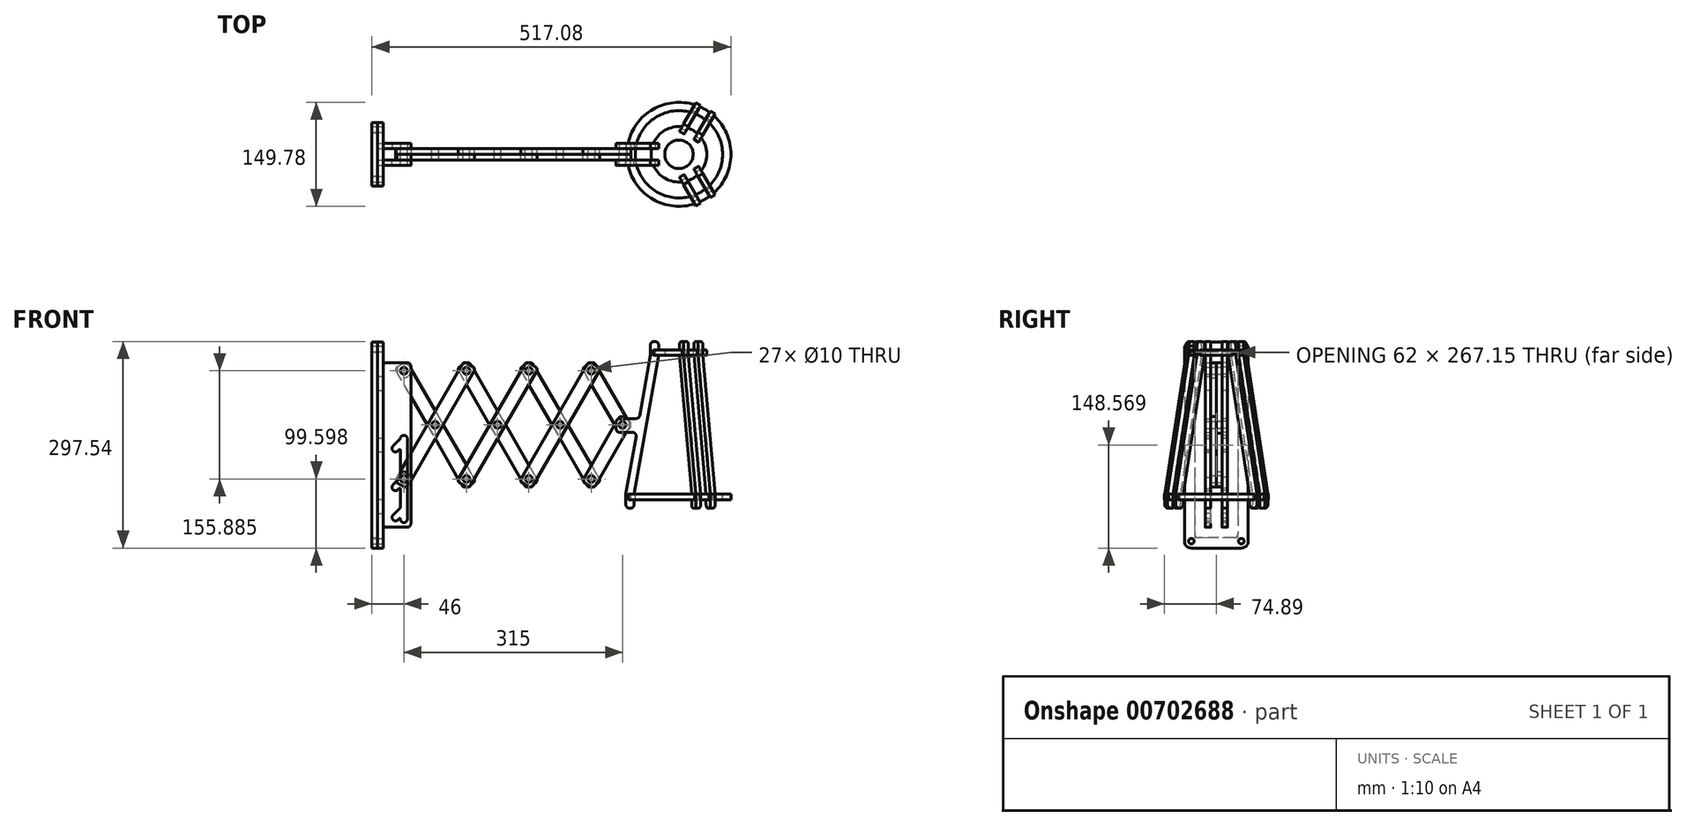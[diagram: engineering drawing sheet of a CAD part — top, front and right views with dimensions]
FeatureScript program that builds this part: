
annotation { "Feature Type Name" : "Feature", "Feature Type Description" : "" }
export const myFeature = defineFeature(function(context is Context, id is Id, definition is map)
    precondition{}
    {
        {
            var Q0;
            Q0=qCreatedBy(makeId("Front.planeOp"),FACE);
            var sketch = newSketch(context, id + "F0", { "sketchPlane" : qUnion([Q0])});
            skLineSegment(sketch, "E0.bottom", {"start": v(54.33, 84.1) * mm, "end": v(45.67, 89.1) * mm});
            skLineSegment(sketch, "E0.top", {"start": v(-45.67, -89.1) * mm, "end": v(-54.33, -84.1) * mm});
            skLineSegment(sketch, "E0.left", {"start": v(56.16, 77.27) * mm, "end": v(-38.84, -87.27) * mm});
            skLineSegment(sketch, "E0.right", {"start": v(38.84, 87.27) * mm, "end": v(-56.16, -77.27) * mm});
            skPoint(sketch, "E0.middle", {"position": v(0, 0) * mm});
            skLineSegment(sketch, "E1", {"start": v(0, 185.82) * mm, "end": v(0, -203.94) * mm, "construction": true});
            skLineSegment(sketch, "E2", {"start": v(-279.88, 0) * mm, "end": v(337.24, 0) * mm, "construction": true});
            skCircle(sketch, "E3", {"center": v(0, 0) * mm, "radius": 5 * mm});
            skCircle(sketch, "E4", {"center": v(45, 77.94) * mm, "radius": 5 * mm});
            skCircle(sketch, "E5.MirrorC", {"center": v(-45, -77.94) * mm, "radius": 5 * mm});
            skPoint(sketch, "E6.visualSharp", {"position": v(41.34, 91.6) * mm});
            skArc(sketch, "E6.filletArc", {"start": v(45.67, 89.1) * mm, "mid": v(41.88, 89.6) * mm, "end": v(38.84, 87.27) * mm});
            skPoint(sketch, "E7.visualSharp", {"position": v(58.66, 81.6) * mm});
            skArc(sketch, "E7.filletArc", {"start": v(56.16, 77.27) * mm, "mid": v(56.66, 81.07) * mm, "end": v(54.33, 84.1) * mm});
            skPoint(sketch, "E8.visualSharp", {"position": v(-41.34, -91.6) * mm});
            skArc(sketch, "E8.filletArc", {"start": v(-45.67, -89.1) * mm, "mid": v(-41.88, -89.6) * mm, "end": v(-38.84, -87.27) * mm});
            skPoint(sketch, "E9.visualSharp", {"position": v(-58.66, -81.6) * mm});
            skArc(sketch, "E9.filletArc", {"start": v(-56.16, -77.27) * mm, "mid": v(-56.66, -81.07) * mm, "end": v(-54.33, -84.1) * mm});
            skSolve(sketch);
        }
        {
            var Q0;
            Q0=makeQuery(id+"F0.imprint","IMPRINT",FACE,{"disambiguationData":[TD([[makeQuery(id+"F0.imprint","IMPRINT",EDGE,{"derivedFrom":sQuery(id+"F0.wireOp",EDGE,"E0.bottom")}),1.0]])]});
            var Q1;
            Q1=makeQuery(id+"F0.imprint","IMPRINT",FACE,{"disambiguationData":[TD([[makeQuery(id+"F0.imprint","IMPRINT",EDGE,{"derivedFrom":sQuery(id+"F0.wireOp",EDGE,"E3")}),-1.0]])]});
            var Q2;
            Q2=makeQuery(id+"F0.imprint","IMPRINT",FACE,{"disambiguationData":[TD([[makeQuery(id+"F0.imprint","IMPRINT",EDGE,{"derivedFrom":sQuery(id+"F0.wireOp",EDGE,"E0.top")}),-1.0]])]});
            var Q3;
            Q3=sQuery(id+"F0.wireOp",EDGE,"E0.right");
            var Q4;
            Q4=sQuery(id+"F0.wireOp",EDGE,"E0.left");
            extrude(context, id + "F1", {"entities" : qUnion([Q0, Q1, Q2]), "surfaceEntities" : qUnion([Q3, Q4]), "depth" : 8 * mm, "offsetDistance" : 25 * mm});
        }
        {
            var Q0;
            Q0=makeQuery(id+"F1.opExtrude","SWEPT_BODY",BODY,{"disambiguationData":[OSD([sQuery(id+"F0.wireOp",EDGE,"E0.bottom"),sQuery(id+"F0.wireOp",EDGE,"E0.top"),sQuery(id+"F0.wireOp",EDGE,"E0.left"),sQuery(id+"F0.wireOp",EDGE,"E0.right"),sQuery(id+"F0.wireOp",EDGE,"E3"),sQuery(id+"F0.wireOp",EDGE,"E4"),sQuery(id+"F0.wireOp",EDGE,"E5.MirrorC"),sQuery(id+"F0.wireOp",EDGE,"E6.filletArc"),sQuery(id+"F0.wireOp",EDGE,"E7.filletArc"),sQuery(id+"F0.wireOp",EDGE,"E8.filletArc"),sQuery(id+"F0.wireOp",EDGE,"E9.filletArc")])]});
            var Q1;
            Q1=qCreatedBy(makeId("Right.planeOp"),FACE);
            mirror(context, id + "F2", {"entities" : qUnion([Q0]), "mirrorPlane" : qUnion([Q1])});
        }
        {
            var Q0;
            Q0=makeQuery(id+"F2.opPattern","COPY",BODY,{"derivedFrom":makeQuery(id+"F1.opExtrude","SWEPT_BODY",BODY,{"disambiguationData":[OSD([sQuery(id+"F0.wireOp",EDGE,"E0.bottom"),sQuery(id+"F0.wireOp",EDGE,"E0.top"),sQuery(id+"F0.wireOp",EDGE,"E0.left"),sQuery(id+"F0.wireOp",EDGE,"E0.right"),sQuery(id+"F0.wireOp",EDGE,"E3"),sQuery(id+"F0.wireOp",EDGE,"E4"),sQuery(id+"F0.wireOp",EDGE,"E5.MirrorC"),sQuery(id+"F0.wireOp",EDGE,"E6.filletArc"),sQuery(id+"F0.wireOp",EDGE,"E7.filletArc"),sQuery(id+"F0.wireOp",EDGE,"E8.filletArc"),sQuery(id+"F0.wireOp",EDGE,"E9.filletArc")])]}),"instanceName":"1"});
            transform(context, id + "F3", {"entities" : qUnion([Q0]), "transformType" : TransformType.TRANSLATION_3D, "dx" : 0 * mm, "dy" : 8 * mm, "dz" : 0 * mm, "makeCopy" : false});
        }
        {
            var Q0;
            Q0=makeQuery(id+"F1.opExtrude","SWEPT_BODY",BODY,{"disambiguationData":[OSD([sQuery(id+"F0.wireOp",EDGE,"E0.bottom"),sQuery(id+"F0.wireOp",EDGE,"E0.top"),sQuery(id+"F0.wireOp",EDGE,"E0.left"),sQuery(id+"F0.wireOp",EDGE,"E0.right"),sQuery(id+"F0.wireOp",EDGE,"E3"),sQuery(id+"F0.wireOp",EDGE,"E4"),sQuery(id+"F0.wireOp",EDGE,"E5.MirrorC"),sQuery(id+"F0.wireOp",EDGE,"E6.filletArc"),sQuery(id+"F0.wireOp",EDGE,"E7.filletArc"),sQuery(id+"F0.wireOp",EDGE,"E8.filletArc"),sQuery(id+"F0.wireOp",EDGE,"E9.filletArc")])]});
            transform(context, id + "F4", {"entities" : qUnion([Q0]), "transformType" : TransformType.TRANSLATION_3D, "dx" : 90 * mm, "dy" : 0 * mm, "dz" : 0 * mm, "makeCopy" : true});
        }
        {
            var Q0;
            Q0=makeQuery(id+"F2.opPattern","COPY",BODY,{"derivedFrom":makeQuery(id+"F1.opExtrude","SWEPT_BODY",BODY,{"disambiguationData":[OSD([sQuery(id+"F0.wireOp",EDGE,"E0.bottom"),sQuery(id+"F0.wireOp",EDGE,"E0.top"),sQuery(id+"F0.wireOp",EDGE,"E0.left"),sQuery(id+"F0.wireOp",EDGE,"E0.right"),sQuery(id+"F0.wireOp",EDGE,"E3"),sQuery(id+"F0.wireOp",EDGE,"E4"),sQuery(id+"F0.wireOp",EDGE,"E5.MirrorC"),sQuery(id+"F0.wireOp",EDGE,"E6.filletArc"),sQuery(id+"F0.wireOp",EDGE,"E7.filletArc"),sQuery(id+"F0.wireOp",EDGE,"E8.filletArc"),sQuery(id+"F0.wireOp",EDGE,"E9.filletArc")])]}),"instanceName":"1"});
            transform(context, id + "F5", {"entities" : qUnion([Q0]), "transformType" : TransformType.TRANSLATION_3D, "dx" : -90 * mm, "dy" : 0 * mm, "dz" : 0 * mm, "makeCopy" : true});
        }
        {
            var Q0;
            Q0=makeQuery(id+"F1.opExtrude","SWEPT_BODY",BODY,{"disambiguationData":[OSD([sQuery(id+"F0.wireOp",EDGE,"E0.bottom"),sQuery(id+"F0.wireOp",EDGE,"E0.top"),sQuery(id+"F0.wireOp",EDGE,"E0.left"),sQuery(id+"F0.wireOp",EDGE,"E0.right"),sQuery(id+"F0.wireOp",EDGE,"E3"),sQuery(id+"F0.wireOp",EDGE,"E4"),sQuery(id+"F0.wireOp",EDGE,"E5.MirrorC"),sQuery(id+"F0.wireOp",EDGE,"E6.filletArc"),sQuery(id+"F0.wireOp",EDGE,"E7.filletArc"),sQuery(id+"F0.wireOp",EDGE,"E8.filletArc"),sQuery(id+"F0.wireOp",EDGE,"E9.filletArc")])]});
            transform(context, id + "F6", {"entities" : qUnion([Q0]), "transformType" : TransformType.TRANSLATION_3D, "dx" : -90 * mm, "dy" : 0 * mm, "dz" : 0 * mm, "makeCopy" : true});
        }
        {
            var Q0;
            Q0=makeQuery(id+"F2.opPattern","COPY",BODY,{"derivedFrom":makeQuery(id+"F1.opExtrude","SWEPT_BODY",BODY,{"disambiguationData":[OSD([sQuery(id+"F0.wireOp",EDGE,"E0.bottom"),sQuery(id+"F0.wireOp",EDGE,"E0.top"),sQuery(id+"F0.wireOp",EDGE,"E0.left"),sQuery(id+"F0.wireOp",EDGE,"E0.right"),sQuery(id+"F0.wireOp",EDGE,"E3"),sQuery(id+"F0.wireOp",EDGE,"E4"),sQuery(id+"F0.wireOp",EDGE,"E5.MirrorC"),sQuery(id+"F0.wireOp",EDGE,"E6.filletArc"),sQuery(id+"F0.wireOp",EDGE,"E7.filletArc"),sQuery(id+"F0.wireOp",EDGE,"E8.filletArc"),sQuery(id+"F0.wireOp",EDGE,"E9.filletArc")])]}),"instanceName":"1"});
            transform(context, id + "F7", {"entities" : qUnion([Q0]), "transformType" : TransformType.TRANSLATION_3D, "dx" : 90 * mm, "dy" : 0 * mm, "dz" : 0 * mm, "makeCopy" : true});
        }
        {
            var Q0;
            Q0=makeQuery(id+"F7.opPattern","COPY",FACE,{"derivedFrom":makeQuery(id+"F2.opPattern","COPY",FACE,{"derivedFrom":makeQuery(id+"F1.opExtrude","CAP_FACE",FACE,{"disambiguationData":[OSD([sQuery(id+"F0.wireOp",EDGE,"E0.bottom"),sQuery(id+"F0.wireOp",EDGE,"E0.top"),sQuery(id+"F0.wireOp",EDGE,"E0.left"),sQuery(id+"F0.wireOp",EDGE,"E0.right"),sQuery(id+"F0.wireOp",EDGE,"E3"),sQuery(id+"F0.wireOp",EDGE,"E4"),sQuery(id+"F0.wireOp",EDGE,"E5.MirrorC"),sQuery(id+"F0.wireOp",EDGE,"E6.filletArc"),sQuery(id+"F0.wireOp",EDGE,"E7.filletArc"),sQuery(id+"F0.wireOp",EDGE,"E8.filletArc"),sQuery(id+"F0.wireOp",EDGE,"E9.filletArc")])],"isStart":true}),"instanceName":"1"}),"instanceName":"1"});
            var sketch = newSketch(context, id + "F8", { "sketchPlane" : qUnion([Q0])});
            skCircle(sketch, "E10.0", {"center": v(135, 77.94) * mm, "radius": 5 * mm});
            skLineSegment(sketch, "E11", {"start": v(130, 89.6) * mm, "end": v(160, 89.6) * mm, "construction": true});
            skPoint(sketch, "E11.startSnap0", {"position": v(41.88, 89.6) * mm});
            skLineSegment(sketch, "E12", {"start": v(22.72, 0) * mm, "end": v(188.2, 0) * mm, "construction": true});
            skLineSegment(sketch, "E13", {"start": v(130, 89.6) * mm, "end": v(160, 89.6) * mm});
            skLineSegment(sketch, "E14", {"start": v(135, 121.8) * mm, "end": v(135, -172.81) * mm, "construction": true});
            skArc(sketch, "E15.0", {"start": v(140, -20) * mm, "mid": v(135, -15) * mm, "end": v(130, -20) * mm});
            skLineSegment(sketch, "E16", {"start": v(95.12, -77.94) * mm, "end": v(188.2, -77.94) * mm, "construction": true});
            skArc(sketch, "E17.MirrorC", {"start": v(140, -135.88) * mm, "mid": v(135, -140.88) * mm, "end": v(130, -135.88) * mm});
            skLineSegment(sketch, "E18", {"start": v(130, -147.54) * mm, "end": v(160, -147.54) * mm});
            skLineSegment(sketch, "E19", {"start": v(125, 84.6) * mm, "end": v(125, -142.54) * mm});
            skLineSegment(sketch, "E20", {"start": v(165, 84.6) * mm, "end": v(165, 69.6) * mm});
            skLineSegment(sketch, "E21", {"start": v(130, -135.88) * mm, "end": v(130, -20) * mm});
            skLineSegment(sketch, "E22.MirrorCS", {"start": v(140, -119.33) * mm, "end": v(140, -92.37) * mm});
            skPoint(sketch, "E23.newPointB", {"position": v(24.22, 89.6) * mm});
            skArc(sketch, "E23.filletArc", {"start": v(130, 89.6) * mm, "mid": v(126.46, 88.14) * mm, "end": v(125, 84.6) * mm});
            skPoint(sketch, "E24.newPointA", {"position": v(188.2, 89.6) * mm});
            skArc(sketch, "E24.filletArc", {"start": v(165, 84.6) * mm, "mid": v(163.54, 88.14) * mm, "end": v(160, 89.6) * mm});
            skPoint(sketch, "E25.visualSharp", {"position": v(125, -147.54) * mm});
            skArc(sketch, "E25.filletArc", {"start": v(125, -142.54) * mm, "mid": v(126.46, -146.08) * mm, "end": v(130, -147.54) * mm});
            skPoint(sketch, "E26.visualSharp", {"position": v(165, -147.54) * mm});
            skArc(sketch, "E26.filletArc", {"start": v(160, -147.54) * mm, "mid": v(163.54, -146.08) * mm, "end": v(165, -142.54) * mm});
            skLineSegment(sketch, "E27", {"start": v(165, 69.6) * mm, "end": v(173, 69.6) * mm});
            skLineSegment(sketch, "E28", {"start": v(173, 69.6) * mm, "end": v(173, 49.6) * mm});
            skLineSegment(sketch, "E29", {"start": v(173, 49.6) * mm, "end": v(165, 49.6) * mm});
            skLineSegment(sketch, "E30", {"start": v(165, -107.54) * mm, "end": v(173, -107.54) * mm});
            skLineSegment(sketch, "E31", {"start": v(173, -107.54) * mm, "end": v(173, -127.54) * mm});
            skLineSegment(sketch, "E32", {"start": v(173, -127.54) * mm, "end": v(165, -127.54) * mm});
            skLineSegment(sketch, "E33.trimOffspring", {"start": v(165, -127.54) * mm, "end": v(165, -142.54) * mm});
            skLineSegment(sketch, "E34.trimOffspring", {"start": v(165, 49.6) * mm, "end": v(165, -18.97) * mm});
            skLineSegment(sketch, "E35", {"start": v(165, -18.97) * mm, "end": v(173, -18.97) * mm});
            skLineSegment(sketch, "E36", {"start": v(173, -18.97) * mm, "end": v(173, -38.97) * mm});
            skLineSegment(sketch, "E37", {"start": v(173, -38.97) * mm, "end": v(165, -38.97) * mm});
            skLineSegment(sketch, "E38.trimOffspring", {"start": v(165, -38.97) * mm, "end": v(165, -107.54) * mm});
            skPoint(sketch, "E39.orphan", {"position": v(165, -28.97) * mm});
            skArc(sketch, "E40", {"start": v(143.5, -93.46) * mm, "mid": v(150.57, -93.46) * mm, "end": v(150.57, -86.4) * mm});
            skLineSegment(sketch, "E41", {"start": v(150.57, -86.4) * mm, "end": v(140, -75.82) * mm});
            skLineSegment(sketch, "E42.MirrorCS", {"start": v(143.5, -93.46) * mm, "end": v(141.7, -91.67) * mm});
            skArc(sketch, "E43.filletArc", {"start": v(141.7, -91.67) * mm, "mid": v(140.62, -91.45) * mm, "end": v(140, -92.37) * mm});
            skArc(sketch, "E44", {"start": v(143.5, -136.97) * mm, "mid": v(150.57, -136.97) * mm, "end": v(150.57, -129.9) * mm});
            skLineSegment(sketch, "E45", {"start": v(150.57, -129.9) * mm, "end": v(140, -119.33) * mm});
            skLineSegment(sketch, "E46.MirrorCS", {"start": v(143.5, -136.97) * mm, "end": v(141.7, -135.18) * mm});
            skArc(sketch, "E47.filletArc", {"start": v(141.7, -135.18) * mm, "mid": v(140.62, -134.96) * mm, "end": v(140, -135.88) * mm});
            skArc(sketch, "E48", {"start": v(143.5, -37.65) * mm, "mid": v(150.57, -37.65) * mm, "end": v(150.57, -30.57) * mm});
            skLineSegment(sketch, "E49", {"start": v(150.57, -30.57) * mm, "end": v(140, -20) * mm});
            skLineSegment(sketch, "E50.MirrorCS", {"start": v(143.5, -37.65) * mm, "end": v(141.7, -35.85) * mm});
            skArc(sketch, "E51.filletArc", {"start": v(141.7, -35.85) * mm, "mid": v(140.62, -35.63) * mm, "end": v(140, -36.56) * mm});
            skLineSegment(sketch, "E52.trimOffspring", {"start": v(140, -75.82) * mm, "end": v(140, -36.56) * mm});
            skSolve(sketch);
        }
        {
            var Q0;
            Q0 = qSketchRegion(id + "F8", true);
            extrude(context, id + "F9", {"entities" : qUnion([Q0]), "depth" : 8 * mm, "offsetDistance" : 25 * mm});
        }
        {
            var Q0;
            Q0=makeQuery(id+"F9.opExtrude","SWEPT_BODY",BODY,{"disambiguationData":[OSD([sQuery(id+"F8.wireOp",EDGE,"E10.0"),sQuery(id+"F8.wireOp",EDGE,"E13"),sQuery(id+"F8.wireOp",EDGE,"E15.0"),sQuery(id+"F8.wireOp",EDGE,"E17.MirrorC"),sQuery(id+"F8.wireOp",EDGE,"E18"),sQuery(id+"F8.wireOp",EDGE,"E19"),sQuery(id+"F8.wireOp",EDGE,"E20"),sQuery(id+"F8.wireOp",EDGE,"E21"),sQuery(id+"F8.wireOp",EDGE,"E22.MirrorCS"),sQuery(id+"F8.wireOp",EDGE,"E23.filletArc"),sQuery(id+"F8.wireOp",EDGE,"E24.filletArc"),sQuery(id+"F8.wireOp",EDGE,"E25.filletArc"),sQuery(id+"F8.wireOp",EDGE,"E26.filletArc")])]});
            var Q1;
            Q1=qCreatedBy(makeId("Front.planeOp"),FACE);
            mirror(context, id + "F10", {"entities" : qUnion([Q0]), "mirrorPlane" : qUnion([Q1])});
        }
        {
            var Q0;
            Q0=makeQuery(id+"F9.opExtrude","SWEPT_FACE",FACE,{"disambiguationData":[OSD([sQuery(id+"F8.wireOp",EDGE,"E34.trimOffspring")])]});
            var sketch = newSketch(context, id + "F11", { "sketchPlane" : qUnion([Q0])});
            skPoint(sketch, "E53.middle", {"position": v(0, 0) * mm});
            skLineSegment(sketch, "E54.0.0", {"start": v(-8, 49.6) * mm, "end": v(-8, 69.6) * mm});
            skLineSegment(sketch, "E54.0.1", {"start": v(-8, 69.6) * mm, "end": v(-16, 69.6) * mm});
            skLineSegment(sketch, "E54.0.2", {"start": v(-16, 69.6) * mm, "end": v(-16, 49.6) * mm});
            skLineSegment(sketch, "E54.0.3", {"start": v(-16, 49.6) * mm, "end": v(-8, 49.6) * mm});
            skLineSegment(sketch, "E55.0.0", {"start": v(8, 69.6) * mm, "end": v(8, 49.6) * mm});
            skLineSegment(sketch, "E55.0.1", {"start": v(8, 49.6) * mm, "end": v(16, 49.6) * mm});
            skLineSegment(sketch, "E55.0.2", {"start": v(16, 49.6) * mm, "end": v(16, 69.6) * mm});
            skLineSegment(sketch, "E55.0.3", {"start": v(16, 69.6) * mm, "end": v(8, 69.6) * mm});
            skLineSegment(sketch, "E56.0.0", {"start": v(-8, -38.97) * mm, "end": v(-8, -18.97) * mm});
            skLineSegment(sketch, "E56.0.1", {"start": v(-8, -18.97) * mm, "end": v(-16, -18.97) * mm});
            skLineSegment(sketch, "E56.0.2", {"start": v(-16, -18.97) * mm, "end": v(-16, -38.97) * mm});
            skLineSegment(sketch, "E56.0.3", {"start": v(-16, -38.97) * mm, "end": v(-8, -38.97) * mm});
            skLineSegment(sketch, "E57.0.0", {"start": v(8, -18.97) * mm, "end": v(8, -38.97) * mm});
            skLineSegment(sketch, "E57.0.1", {"start": v(8, -38.97) * mm, "end": v(16, -38.97) * mm});
            skLineSegment(sketch, "E57.0.2", {"start": v(16, -38.97) * mm, "end": v(16, -18.97) * mm});
            skLineSegment(sketch, "E57.0.3", {"start": v(16, -18.97) * mm, "end": v(8, -18.97) * mm});
            skLineSegment(sketch, "E58.0.0", {"start": v(-8, -127.54) * mm, "end": v(-8, -107.54) * mm});
            skLineSegment(sketch, "E58.0.1", {"start": v(-8, -107.54) * mm, "end": v(-16, -107.54) * mm});
            skLineSegment(sketch, "E58.0.2", {"start": v(-16, -107.54) * mm, "end": v(-16, -127.54) * mm});
            skLineSegment(sketch, "E58.0.3", {"start": v(-16, -127.54) * mm, "end": v(-8, -127.54) * mm});
            skLineSegment(sketch, "E59.0.0", {"start": v(8, -107.54) * mm, "end": v(8, -127.54) * mm});
            skLineSegment(sketch, "E59.0.1", {"start": v(8, -127.54) * mm, "end": v(16, -127.54) * mm});
            skLineSegment(sketch, "E59.0.2", {"start": v(16, -127.54) * mm, "end": v(16, -107.54) * mm});
            skLineSegment(sketch, "E59.0.3", {"start": v(16, -107.54) * mm, "end": v(8, -107.54) * mm});
            skLineSegment(sketch, "E60", {"start": v(46, 109.6) * mm, "end": v(46, -167.54) * mm});
            skLineSegment(sketch, "E61", {"start": v(-36, 119.6) * mm, "end": v(36, 119.6) * mm});
            skLineSegment(sketch, "E62", {"start": v(-36, -177.54) * mm, "end": v(36, -177.54) * mm});
            skLineSegment(sketch, "E63.MirrorCS", {"start": v(-46, 109.6) * mm, "end": v(-46, -167.54) * mm});
            skPoint(sketch, "E64.visualSharp", {"position": v(-46, 119.6) * mm});
            skArc(sketch, "E64.filletArc", {"start": v(-36, 119.6) * mm, "mid": v(-43.07, 116.67) * mm, "end": v(-46, 109.6) * mm});
            skPoint(sketch, "E65.visualSharp", {"position": v(46, 119.6) * mm});
            skArc(sketch, "E65.filletArc", {"start": v(46, 109.6) * mm, "mid": v(43.07, 116.67) * mm, "end": v(36, 119.6) * mm});
            skPoint(sketch, "E66.visualSharp", {"position": v(-46, -177.54) * mm});
            skArc(sketch, "E66.filletArc", {"start": v(-46, -167.54) * mm, "mid": v(-43.07, -174.62) * mm, "end": v(-36, -177.54) * mm});
            skPoint(sketch, "E67.visualSharp", {"position": v(46, -177.54) * mm});
            skArc(sketch, "E67.filletArc", {"start": v(36, -177.54) * mm, "mid": v(43.07, -174.62) * mm, "end": v(46, -167.54) * mm});
            skCircle(sketch, "E68", {"center": v(-36, 109.6) * mm, "radius": 4 * mm});
            skCircle(sketch, "E69", {"center": v(36, 109.6) * mm, "radius": 4 * mm});
            skCircle(sketch, "E70", {"center": v(-36, -167.54) * mm, "radius": 4 * mm});
            skCircle(sketch, "E71", {"center": v(36, -167.54) * mm, "radius": 4 * mm});
            skSolve(sketch);
        }
        {
            var Q0;
            Q0 = qSketchRegion(id + "F11", true);
            extrude(context, id + "F12", {"entities" : qUnion([Q0]), "depth" : 8 * mm, "offsetDistance" : 25 * mm});
        }
        {
            var Q0;
            Q0=makeQuery(id+"F12.opExtrude","CAP_FACE",FACE,{"disambiguationData":[OSD([sQuery(id+"F11.wireOp",EDGE,"E54.0.0"),sQuery(id+"F11.wireOp",EDGE,"E54.0.1"),sQuery(id+"F11.wireOp",EDGE,"E54.0.2"),sQuery(id+"F11.wireOp",EDGE,"E54.0.3"),sQuery(id+"F11.wireOp",EDGE,"E55.0.0"),sQuery(id+"F11.wireOp",EDGE,"E55.0.1"),sQuery(id+"F11.wireOp",EDGE,"E55.0.2"),sQuery(id+"F11.wireOp",EDGE,"E55.0.3"),sQuery(id+"F11.wireOp",EDGE,"E56.0.0"),sQuery(id+"F11.wireOp",EDGE,"E56.0.1"),sQuery(id+"F11.wireOp",EDGE,"E56.0.2"),sQuery(id+"F11.wireOp",EDGE,"E56.0.3"),sQuery(id+"F11.wireOp",EDGE,"E57.0.0"),sQuery(id+"F11.wireOp",EDGE,"E57.0.1"),sQuery(id+"F11.wireOp",EDGE,"E57.0.2"),sQuery(id+"F11.wireOp",EDGE,"E57.0.3"),sQuery(id+"F11.wireOp",EDGE,"E58.0.0"),sQuery(id+"F11.wireOp",EDGE,"E58.0.1"),sQuery(id+"F11.wireOp",EDGE,"E58.0.2"),sQuery(id+"F11.wireOp",EDGE,"E58.0.3"),sQuery(id+"F11.wireOp",EDGE,"E59.0.0"),sQuery(id+"F11.wireOp",EDGE,"E59.0.1"),sQuery(id+"F11.wireOp",EDGE,"E59.0.2"),sQuery(id+"F11.wireOp",EDGE,"E59.0.3"),sQuery(id+"F11.wireOp",EDGE,"E60"),sQuery(id+"F11.wireOp",EDGE,"E61"),sQuery(id+"F11.wireOp",EDGE,"E62"),sQuery(id+"F11.wireOp",EDGE,"E63.MirrorCS"),sQuery(id+"F11.wireOp",EDGE,"E64.filletArc"),sQuery(id+"F11.wireOp",EDGE,"E65.filletArc"),sQuery(id+"F11.wireOp",EDGE,"E66.filletArc"),sQuery(id+"F11.wireOp",EDGE,"E67.filletArc"),sQuery(id+"F11.wireOp",EDGE,"E68"),sQuery(id+"F11.wireOp",EDGE,"E69"),sQuery(id+"F11.wireOp",EDGE,"E70"),sQuery(id+"F11.wireOp",EDGE,"E71")])],"isStart":false});
            var sketch = newSketch(context, id + "F13", { "sketchPlane" : qUnion([Q0])});
            skArc(sketch, "E72.0.0", {"start": v(-36, 119.6) * mm, "mid": v(-43.07, 116.67) * mm, "end": v(-46, 109.6) * mm});
            skLineSegment(sketch, "E72.0.1", {"start": v(-46, 109.6) * mm, "end": v(-46, -167.54) * mm});
            skArc(sketch, "E72.0.2", {"start": v(-46, -167.54) * mm, "mid": v(-43.07, -174.62) * mm, "end": v(-36, -177.54) * mm});
            skLineSegment(sketch, "E72.0.3", {"start": v(-36, -177.54) * mm, "end": v(36, -177.54) * mm});
            skArc(sketch, "E72.0.4", {"start": v(36, -177.54) * mm, "mid": v(43.07, -174.62) * mm, "end": v(46, -167.54) * mm});
            skLineSegment(sketch, "E72.0.5", {"start": v(46, -167.54) * mm, "end": v(46, 109.6) * mm});
            skArc(sketch, "E72.0.6", {"start": v(46, 109.6) * mm, "mid": v(43.07, 116.67) * mm, "end": v(36, 119.6) * mm});
            skLineSegment(sketch, "E72.0.7", {"start": v(36, 119.6) * mm, "end": v(-36, 119.6) * mm});
            skCircle(sketch, "E73.0", {"center": v(-36, 109.6) * mm, "radius": 4 * mm});
            skCircle(sketch, "E74.0", {"center": v(36, 109.6) * mm, "radius": 4 * mm});
            skCircle(sketch, "E75.0", {"center": v(-36, -167.54) * mm, "radius": 4 * mm});
            skCircle(sketch, "E76.0", {"center": v(36, -167.54) * mm, "radius": 4 * mm});
            skLineSegment(sketch, "E77.bottom", {"start": v(-26, 104.6) * mm, "end": v(26, 104.6) * mm});
            skLineSegment(sketch, "E77.top", {"start": v(-26, -162.54) * mm, "end": v(26, -162.54) * mm});
            skLineSegment(sketch, "E77.left", {"start": v(-31, 99.6) * mm, "end": v(-31, -157.54) * mm});
            skLineSegment(sketch, "E77.right", {"start": v(31, 99.6) * mm, "end": v(31, -157.54) * mm});
            skPoint(sketch, "E78.visualSharp", {"position": v(-31, 104.6) * mm});
            skArc(sketch, "E78.filletArc", {"start": v(-26, 104.6) * mm, "mid": v(-29.54, 103.14) * mm, "end": v(-31, 99.6) * mm});
            skPoint(sketch, "E79.visualSharp", {"position": v(31, 104.6) * mm});
            skArc(sketch, "E79.filletArc", {"start": v(31, 99.6) * mm, "mid": v(29.54, 103.14) * mm, "end": v(26, 104.6) * mm});
            skPoint(sketch, "E80.visualSharp", {"position": v(-31, -162.54) * mm});
            skArc(sketch, "E80.filletArc", {"start": v(-31, -157.54) * mm, "mid": v(-29.54, -161.08) * mm, "end": v(-26, -162.54) * mm});
            skPoint(sketch, "E81.visualSharp", {"position": v(31, -162.54) * mm});
            skArc(sketch, "E81.filletArc", {"start": v(26, -162.54) * mm, "mid": v(29.54, -161.08) * mm, "end": v(31, -157.54) * mm});
            skSolve(sketch);
        }
        {
            var Q0;
            Q0 = qSketchRegion(id + "F13", true);
            extrude(context, id + "F14", {"entities" : qUnion([Q0]), "depth" : 8 * mm, "offsetDistance" : 25 * mm});
        }
        {
            var Q0;
            Q0=makeQuery(id+"F6.opPattern","COPY",FACE,{"derivedFrom":makeQuery(id+"F1.opExtrude","CAP_FACE",FACE,{"disambiguationData":[OSD([sQuery(id+"F0.wireOp",EDGE,"E0.bottom"),sQuery(id+"F0.wireOp",EDGE,"E0.top"),sQuery(id+"F0.wireOp",EDGE,"E0.left"),sQuery(id+"F0.wireOp",EDGE,"E0.right"),sQuery(id+"F0.wireOp",EDGE,"E3"),sQuery(id+"F0.wireOp",EDGE,"E4"),sQuery(id+"F0.wireOp",EDGE,"E5.MirrorC"),sQuery(id+"F0.wireOp",EDGE,"E6.filletArc"),sQuery(id+"F0.wireOp",EDGE,"E7.filletArc"),sQuery(id+"F0.wireOp",EDGE,"E8.filletArc"),sQuery(id+"F0.wireOp",EDGE,"E9.filletArc")])],"isStart":true}),"instanceName":"1"});
            var sketch = newSketch(context, id + "F15", { "sketchPlane" : qUnion([Q0])});
            skCircle(sketch, "E82.0", {"center": v(135, -77.94) * mm, "radius": 5 * mm});
            skCircle(sketch, "E83", {"center": v(135, -77.94) * mm, "radius": 10 * mm});
            skSolve(sketch);
        }
        {
            var Q0;
            Q0 = qSketchRegion(id + "F15", true);
            extrude(context, id + "F16", {"entities" : qUnion([Q0]), "depth" : 8 * mm, "offsetDistance" : 25 * mm});
        }
        {
            var Q0;
            Q0=makeQuery(id+"F5.opPattern","COPY",FACE,{"derivedFrom":makeQuery(id+"F2.opPattern","COPY",FACE,{"derivedFrom":makeQuery(id+"F1.opExtrude","CAP_FACE",FACE,{"disambiguationData":[OSD([sQuery(id+"F0.wireOp",EDGE,"E0.bottom"),sQuery(id+"F0.wireOp",EDGE,"E0.top"),sQuery(id+"F0.wireOp",EDGE,"E0.left"),sQuery(id+"F0.wireOp",EDGE,"E0.right"),sQuery(id+"F0.wireOp",EDGE,"E3"),sQuery(id+"F0.wireOp",EDGE,"E4"),sQuery(id+"F0.wireOp",EDGE,"E5.MirrorC"),sQuery(id+"F0.wireOp",EDGE,"E6.filletArc"),sQuery(id+"F0.wireOp",EDGE,"E7.filletArc"),sQuery(id+"F0.wireOp",EDGE,"E8.filletArc"),sQuery(id+"F0.wireOp",EDGE,"E9.filletArc")])],"isStart":false}),"instanceName":"1"}),"instanceName":"1"});
            var sketch = newSketch(context, id + "F17", { "sketchPlane" : qUnion([Q0])});
            skCircle(sketch, "E84.0", {"center": v(-135, 77.94) * mm, "radius": 5 * mm});
            skCircle(sketch, "E85", {"center": v(-135, 77.94) * mm, "radius": 10 * mm});
            skSolve(sketch);
        }
        {
            var Q0;
            Q0 = qSketchRegion(id + "F17", true);
            extrude(context, id + "F18", {"entities" : qUnion([Q0]), "depth" : 8 * mm, "offsetDistance" : 25 * mm});
        }
        {
            var Q0;
            Q0=makeQuery(id+"F2.opPattern","COPY",FACE,{"derivedFrom":makeQuery(id+"F1.opExtrude","CAP_FACE",FACE,{"disambiguationData":[OSD([sQuery(id+"F0.wireOp",EDGE,"E0.bottom"),sQuery(id+"F0.wireOp",EDGE,"E0.top"),sQuery(id+"F0.wireOp",EDGE,"E0.left"),sQuery(id+"F0.wireOp",EDGE,"E0.right"),sQuery(id+"F0.wireOp",EDGE,"E3"),sQuery(id+"F0.wireOp",EDGE,"E4"),sQuery(id+"F0.wireOp",EDGE,"E5.MirrorC"),sQuery(id+"F0.wireOp",EDGE,"E6.filletArc"),sQuery(id+"F0.wireOp",EDGE,"E7.filletArc"),sQuery(id+"F0.wireOp",EDGE,"E8.filletArc"),sQuery(id+"F0.wireOp",EDGE,"E9.filletArc")])],"isStart":false}),"instanceName":"1"});
            var sketch = newSketch(context, id + "F19", { "sketchPlane" : qUnion([Q0])});
            skLineSegment(sketch, "E86.top", {"start": v(134.33, -89.1) * mm, "end": v(125.67, -84.1) * mm});
            skLineSegment(sketch, "E86.left", {"start": v(191.55, 0) * mm, "end": v(141.16, -87.27) * mm});
            skLineSegment(sketch, "E86.right", {"start": v(173.84, 9.33) * mm, "end": v(123.84, -77.27) * mm});
            skPoint(sketch, "E86.middle", {"position": v(180, 0) * mm});
            skLineSegment(sketch, "E87", {"start": v(180, 185.82) * mm, "end": v(180, -203.94) * mm, "construction": true});
            skLineSegment(sketch, "E88", {"start": v(-99.88, 0) * mm, "end": v(517.24, 0) * mm, "construction": true});
            skCircle(sketch, "E89.MirrorC", {"center": v(135, -77.94) * mm, "radius": 5 * mm});
            skPoint(sketch, "E90.visualSharp", {"position": v(138.66, -91.6) * mm});
            skArc(sketch, "E90.filletArc", {"start": v(134.33, -89.1) * mm, "mid": v(138.12, -89.6) * mm, "end": v(141.16, -87.27) * mm});
            skPoint(sketch, "E91.visualSharp", {"position": v(121.34, -81.6) * mm});
            skArc(sketch, "E91.filletArc", {"start": v(123.84, -77.27) * mm, "mid": v(123.34, -81.07) * mm, "end": v(125.67, -84.1) * mm});
            skLineSegment(sketch, "E92.bottom", {"start": v(189.33, 6.16) * mm, "end": v(180.67, 11.16) * mm});
            skCircle(sketch, "E93", {"center": v(180, 0) * mm, "radius": 5 * mm});
            skArc(sketch, "E94.filletArc", {"start": v(180.67, 11.16) * mm, "mid": v(176.88, 11.66) * mm, "end": v(173.84, 9.33) * mm});
            skArc(sketch, "E95.filletArc", {"start": v(191.16, -0.67) * mm, "mid": v(191.66, 3.12) * mm, "end": v(189.33, 6.16) * mm});
            skSolve(sketch);
        }
        {
            var Q0;
            Q0 = qSketchRegion(id + "F19", true);
            extrude(context, id + "F20", {"entities" : qUnion([Q0]), "operationType" : NewBodyOperationType.ADD, "depth" : 8 * mm, "offsetDistance" : 25 * mm});
        }
        {
            var Q0;
            Q0=makeQuery(id+"F4.opPattern","COPY",FACE,{"derivedFrom":makeQuery(id+"F1.opExtrude","CAP_FACE",FACE,{"disambiguationData":[OSD([sQuery(id+"F0.wireOp",EDGE,"E0.bottom"),sQuery(id+"F0.wireOp",EDGE,"E0.top"),sQuery(id+"F0.wireOp",EDGE,"E0.left"),sQuery(id+"F0.wireOp",EDGE,"E0.right"),sQuery(id+"F0.wireOp",EDGE,"E3"),sQuery(id+"F0.wireOp",EDGE,"E4"),sQuery(id+"F0.wireOp",EDGE,"E5.MirrorC"),sQuery(id+"F0.wireOp",EDGE,"E6.filletArc"),sQuery(id+"F0.wireOp",EDGE,"E7.filletArc"),sQuery(id+"F0.wireOp",EDGE,"E8.filletArc"),sQuery(id+"F0.wireOp",EDGE,"E9.filletArc")])],"isStart":true}),"instanceName":"1"});
            var sketch = newSketch(context, id + "F21", { "sketchPlane" : qUnion([Q0])});
            skLineSegment(sketch, "E96.top", {"start": v(-180.67, -11.16) * mm, "end": v(-189.33, -6.16) * mm});
            skLineSegment(sketch, "E96.left", {"start": v(-123.45, 77.94) * mm, "end": v(-173.84, -9.33) * mm});
            skLineSegment(sketch, "E96.right", {"start": v(-141.16, 87.27) * mm, "end": v(-191.16, 0.67) * mm});
            skPoint(sketch, "E96.middle", {"position": v(-135, 77.94) * mm});
            skLineSegment(sketch, "E97", {"start": v(-135, 263.76) * mm, "end": v(-135, -126) * mm, "construction": true});
            skLineSegment(sketch, "E98", {"start": v(-414.88, 77.94) * mm, "end": v(202.24, 77.94) * mm, "construction": true});
            skCircle(sketch, "E99.MirrorC", {"center": v(-180, 0) * mm, "radius": 5 * mm});
            skPoint(sketch, "E100.visualSharp", {"position": v(-176.34, -13.66) * mm});
            skArc(sketch, "E100.filletArc", {"start": v(-180.67, -11.16) * mm, "mid": v(-176.88, -11.66) * mm, "end": v(-173.84, -9.33) * mm});
            skPoint(sketch, "E101.visualSharp", {"position": v(-193.66, -3.66) * mm});
            skArc(sketch, "E101.filletArc", {"start": v(-191.16, 0.67) * mm, "mid": v(-191.66, -3.12) * mm, "end": v(-189.33, -6.16) * mm});
            skLineSegment(sketch, "E102.bottom", {"start": v(-125.67, 84.1) * mm, "end": v(-134.33, 89.1) * mm});
            skCircle(sketch, "E103", {"center": v(-135, 77.94) * mm, "radius": 5 * mm});
            skArc(sketch, "E104.filletArc", {"start": v(-134.33, 89.1) * mm, "mid": v(-138.12, 89.6) * mm, "end": v(-141.16, 87.27) * mm});
            skArc(sketch, "E105.filletArc", {"start": v(-123.84, 77.27) * mm, "mid": v(-123.34, 81.07) * mm, "end": v(-125.67, 84.1) * mm});
            skSolve(sketch);
        }
        {
            var Q0;
            Q0 = qSketchRegion(id + "F21", true);
            extrude(context, id + "F22", {"entities" : qUnion([Q0]), "depth" : 8 * mm, "offsetDistance" : 25 * mm});
        }
        {
            var Q0;
            Q0=qCreatedBy(makeId("Top.planeOp"),FACE);
            cPlane(context, id + "F23", {"entities" : qUnion([Q0]), "cplaneType" : CPlaneType.OFFSET, "offset" : 100 * mm, "width" : 150 * mm, "height" : 150 * mm});
        }
        {
            var Q0;
            Q0=qCreatedBy(id+"F23.planeOp",FACE);
            var sketch = newSketch(context, id + "F24", { "sketchPlane" : qUnion([Q0])});
            skLineSegment(sketch, "E106", {"start": v(259.2, -71.82) * mm, "end": v(259.2, 43.7) * mm, "construction": true});
            skPoint(sketch, "E107.centerSnap0", {"position": v(259.2, -8) * mm});
            skCircle(sketch, "E108", {"center": v(259.2, 0) * mm, "radius": 20.5 * mm});
            skLineSegment(sketch, "E109", {"start": v(166.47, 0) * mm, "end": v(330.06, 0) * mm, "construction": true});
            skLineSegment(sketch, "E110", {"start": v(220, -8) * mm, "end": v(225, -8) * mm});
            skLineSegment(sketch, "E111", {"start": v(225, -8) * mm, "end": v(225, -16) * mm});
            skLineSegment(sketch, "E112", {"start": v(225, -16) * mm, "end": v(222.53, -16) * mm});
            skLineSegment(sketch, "E113.MirrorCS", {"start": v(220, 8) * mm, "end": v(225, 8) * mm});
            skLineSegment(sketch, "E114.MirrorCS", {"start": v(225, 8) * mm, "end": v(225, 16) * mm});
            skLineSegment(sketch, "E115.MirrorCS", {"start": v(225, 16) * mm, "end": v(222.53, 16) * mm});
            skLineSegment(sketch, "E116.1.1", {"start": v(269.36, -33.61) * mm, "end": v(262.43, -37.61) * mm});
            skLineSegment(sketch, "E116.1.2", {"start": v(271.86, -37.94) * mm, "end": v(269.36, -33.61) * mm});
            skLineSegment(sketch, "E116.1.3", {"start": v(262.43, -37.61) * mm, "end": v(263.67, -39.75) * mm});
            skLineSegment(sketch, "E116.1.4", {"start": v(290.14, -21.61) * mm, "end": v(291.38, -23.75) * mm});
            skLineSegment(sketch, "E116.1.5", {"start": v(283.22, -25.61) * mm, "end": v(290.14, -21.61) * mm});
            skLineSegment(sketch, "E116.1.6", {"start": v(285.72, -29.94) * mm, "end": v(283.22, -25.61) * mm});
            skLineSegment(sketch, "E116.2.1", {"start": v(283.22, 25.61) * mm, "end": v(290.14, 21.61) * mm});
            skLineSegment(sketch, "E116.2.2", {"start": v(285.72, 29.94) * mm, "end": v(283.22, 25.61) * mm});
            skLineSegment(sketch, "E116.2.3", {"start": v(290.14, 21.61) * mm, "end": v(291.38, 23.75) * mm});
            skLineSegment(sketch, "E116.2.4", {"start": v(262.43, 37.61) * mm, "end": v(263.67, 39.75) * mm});
            skLineSegment(sketch, "E116.2.5", {"start": v(269.36, 33.61) * mm, "end": v(262.43, 37.61) * mm});
            skLineSegment(sketch, "E116.2.6", {"start": v(271.86, 37.94) * mm, "end": v(269.36, 33.61) * mm});
            skArc(sketch, "E117", {"start": v(263.67, 39.75) * mm, "mid": v(239.2, 34.64) * mm, "end": v(222.53, 16) * mm});
            skArc(sketch, "E118.trimOffspring", {"start": v(285.72, 29.94) * mm, "mid": v(279.2, 34.64) * mm, "end": v(271.86, 37.94) * mm});
            skArc(sketch, "E119.trimOffspring", {"start": v(291.38, -23.75) * mm, "mid": v(299.2, 0) * mm, "end": v(291.38, 23.75) * mm});
            skArc(sketch, "E120.trimOffspring", {"start": v(271.86, -37.94) * mm, "mid": v(279.2, -34.64) * mm, "end": v(285.72, -29.94) * mm});
            skArc(sketch, "E121.trimOffspring", {"start": v(222.53, -16) * mm, "mid": v(239.2, -34.64) * mm, "end": v(263.67, -39.75) * mm});
            skArc(sketch, "E122.trimOffspring", {"start": v(220, 8) * mm, "mid": v(219.2, 0) * mm, "end": v(220, -8) * mm});
            skSolve(sketch);
        }
        {
            var Q0;
            Q0=makeQuery(id+"F24.imprint","IMPRINT",FACE,{"disambiguationData":[TD([[makeQuery(id+"F24.imprint","IMPRINT",EDGE,{"derivedFrom":sQuery(id+"F24.wireOp",EDGE,"E110")}),1.0]])]});
            var Q1;
            Q1=sQuery(id+"F24.wireOp",EDGE,"E111");
            extrude(context, id + "F25", {"entities" : qUnion([Q0]), "surfaceEntities" : qUnion([Q1]), "depth" : 8 * mm, "offsetDistance" : 25 * mm});
        }
        {
            var Q0;
            Q0=qCreatedBy(makeId("Top.planeOp"),FACE);
            cPlane(context, id + "F26", {"entities" : qUnion([Q0]), "cplaneType" : CPlaneType.OFFSET, "offset" : 100 * mm, "oppositeDirection" : true, "width" : 150 * mm, "height" : 150 * mm});
        }
        {
            var Q0;
            Q0=qCreatedBy(id+"F26.planeOp",FACE);
            var sketch = newSketch(context, id + "F27", { "sketchPlane" : qUnion([Q0])});
            skArc(sketch, "E123", {"start": v(186.04, -16) * mm, "mid": v(221.75, -64.85) * mm, "end": v(281.91, -71.36) * mm});
            skPoint(sketch, "E124.orphan", {"position": v(184.73, -8) * mm});
            skLineSegment(sketch, "E125.0", {"start": v(189.73, -8) * mm, "end": v(189.73, -16) * mm});
            skLineSegment(sketch, "E126.0.12", {"start": v(189.73, 16) * mm, "end": v(189.73, 8) * mm});
            skLineSegment(sketch, "E126.0.13", {"start": v(189.73, 8) * mm, "end": v(184.73, 8) * mm});
            skLineSegment(sketch, "E126.0.15", {"start": v(184.73, -8) * mm, "end": v(189.73, -8) * mm});
            skLineSegment(sketch, "E127", {"start": v(189.73, -16) * mm, "end": v(186.04, -16) * mm});
            skLineSegment(sketch, "E128", {"start": v(189.73, 16) * mm, "end": v(186.04, 16) * mm});
            skLineSegment(sketch, "E129.1.0", {"start": v(280.06, -68.15) * mm, "end": v(281.91, -71.36) * mm});
            skLineSegment(sketch, "E129.1.1", {"start": v(280.06, -68.15) * mm, "end": v(287, -64.15) * mm});
            skLineSegment(sketch, "E129.1.2", {"start": v(287, -64.15) * mm, "end": v(289.5, -68.48) * mm});
            skLineSegment(sketch, "E129.1.3", {"start": v(303.35, -60.48) * mm, "end": v(300.85, -56.15) * mm});
            skLineSegment(sketch, "E129.1.4", {"start": v(300.85, -56.15) * mm, "end": v(307.78, -52.15) * mm});
            skLineSegment(sketch, "E129.1.5", {"start": v(307.78, -52.15) * mm, "end": v(309.63, -55.36) * mm});
            skLineSegment(sketch, "E129.2.0", {"start": v(307.78, 52.15) * mm, "end": v(309.63, 55.36) * mm});
            skLineSegment(sketch, "E129.2.1", {"start": v(307.78, 52.15) * mm, "end": v(300.85, 56.15) * mm});
            skLineSegment(sketch, "E129.2.2", {"start": v(300.85, 56.15) * mm, "end": v(303.35, 60.48) * mm});
            skLineSegment(sketch, "E129.2.3", {"start": v(289.5, 68.48) * mm, "end": v(287, 64.15) * mm});
            skLineSegment(sketch, "E129.2.4", {"start": v(287, 64.15) * mm, "end": v(280.06, 68.15) * mm});
            skLineSegment(sketch, "E129.2.5", {"start": v(280.06, 68.15) * mm, "end": v(281.91, 71.36) * mm});
            skCircle(sketch, "E130.0", {"center": v(259.2, 0) * mm, "radius": 62.89 * mm});
            skArc(sketch, "E131.trimOffspring", {"start": v(184.73, 8) * mm, "mid": v(184.3, 0) * mm, "end": v(184.73, -8) * mm});
            skArc(sketch, "E132.trimOffspring", {"start": v(289.5, -68.48) * mm, "mid": v(296.63, -64.85) * mm, "end": v(303.35, -60.48) * mm});
            skArc(sketch, "E133.trimOffspring", {"start": v(309.63, -55.36) * mm, "mid": v(334.08, 0) * mm, "end": v(309.63, 55.36) * mm});
            skArc(sketch, "E134.trimOffspring", {"start": v(303.35, 60.48) * mm, "mid": v(296.63, 64.85) * mm, "end": v(289.5, 68.48) * mm});
            skArc(sketch, "E135.trimOffspring", {"start": v(281.91, 71.36) * mm, "mid": v(221.75, 64.85) * mm, "end": v(186.04, 16) * mm});
            skSolve(sketch);
        }
        {
            var Q0;
            Q0 = qSketchRegion(id + "F27", true);
            extrude(context, id + "F28", {"entities" : qUnion([Q0]), "oppositeDirection" : true, "depth" : 8 * mm, "offsetDistance" : 25 * mm});
        }
        {
            var Q0;
            Q0=makeQuery(id+"F20.opExtrude","CAP_FACE",FACE,{"disambiguationData":[OSD([sQuery(id+"F19.wireOp",EDGE,"E86.top"),sQuery(id+"F19.wireOp",EDGE,"E86.left"),sQuery(id+"F19.wireOp",EDGE,"E86.right"),sQuery(id+"F19.wireOp",EDGE,"E89.MirrorC"),sQuery(id+"F19.wireOp",EDGE,"E90.filletArc"),sQuery(id+"F19.wireOp",EDGE,"E91.filletArc"),sQuery(id+"F19.wireOp",EDGE,"E92.bottom"),sQuery(id+"F19.wireOp",EDGE,"E93"),sQuery(id+"F19.wireOp",EDGE,"E94.filletArc"),sQuery(id+"F19.wireOp",EDGE,"E95.filletArc")])],"isStart":false});
            var sketch = newSketch(context, id + "F29", { "sketchPlane" : qUnion([Q0])});
            skLineSegment(sketch, "E136.top", {"start": v(170.8, -5.84) * mm, "end": v(170.8, 4.16) * mm});
            skLineSegment(sketch, "E136.left", {"start": v(194.5, -10.84) * mm, "end": v(175.8, -10.84) * mm});
            skLineSegment(sketch, "E136.right", {"start": v(199.79, 9.16) * mm, "end": v(175.8, 9.16) * mm});
            skCircle(sketch, "E137.MirrorC", {"center": v(180, 0) * mm, "radius": 5 * mm});
            skPoint(sketch, "E138.visualSharp", {"position": v(170.8, -10.84) * mm});
            skArc(sketch, "E138.filletArc", {"start": v(170.8, -5.84) * mm, "mid": v(172.26, -9.37) * mm, "end": v(175.8, -10.84) * mm});
            skPoint(sketch, "E139.visualSharp", {"position": v(170.8, 9.16) * mm});
            skArc(sketch, "E139.filletArc", {"start": v(175.8, 9.16) * mm, "mid": v(172.26, 7.7) * mm, "end": v(170.8, 4.16) * mm});
            skPoint(sketch, "E140.MirrorP", {"position": v(261.82, 12.85) * mm});
            skLineSegment(sketch, "E141", {"start": v(220, 100) * mm, "end": v(204.71, 13.3) * mm});
            skLineSegment(sketch, "E142.trimOffspring", {"start": v(199.42, -16.7) * mm, "end": v(184.73, -100) * mm});
            skPoint(sketch, "E143.start.orphan", {"position": v(300, 100) * mm});
            skLineSegment(sketch, "E144", {"start": v(220, 100) * mm, "end": v(220, 115) * mm});
            skLineSegment(sketch, "E145", {"start": v(225, 120) * mm, "end": v(227, 120) * mm});
            skLineSegment(sketch, "E146", {"start": v(232, 115) * mm, "end": v(232, 108) * mm});
            skLineSegment(sketch, "E147", {"start": v(232, 100) * mm, "end": v(196.73, -100) * mm});
            skLineSegment(sketch, "E148", {"start": v(196.73, -108) * mm, "end": v(196.73, -115) * mm});
            skLineSegment(sketch, "E149", {"start": v(191.73, -120) * mm, "end": v(189.73, -120) * mm});
            skLineSegment(sketch, "E150", {"start": v(184.73, -100) * mm, "end": v(184.73, -115) * mm});
            skLineSegment(sketch, "E151", {"start": v(232, 108) * mm, "end": v(227, 108) * mm});
            skLineSegment(sketch, "E152", {"start": v(227, 108) * mm, "end": v(227, 100) * mm});
            skLineSegment(sketch, "E153", {"start": v(227, 100) * mm, "end": v(232, 100) * mm});
            skPoint(sketch, "E154.visualSharp", {"position": v(220, 120) * mm});
            skArc(sketch, "E154.filletArc", {"start": v(225, 120) * mm, "mid": v(221.46, 118.54) * mm, "end": v(220, 115) * mm});
            skPoint(sketch, "E155.visualSharp", {"position": v(232, 120) * mm});
            skArc(sketch, "E155.filletArc", {"start": v(232, 115) * mm, "mid": v(230.54, 118.54) * mm, "end": v(227, 120) * mm});
            skPoint(sketch, "E156.visualSharp", {"position": v(203.98, 9.16) * mm});
            skArc(sketch, "E156.filletArc", {"start": v(199.79, 9.16) * mm, "mid": v(203, 10.33) * mm, "end": v(204.71, 13.3) * mm});
            skPoint(sketch, "E157.visualSharp", {"position": v(200.46, -10.84) * mm});
            skArc(sketch, "E157.filletArc", {"start": v(199.42, -16.7) * mm, "mid": v(198.33, -12.62) * mm, "end": v(194.5, -10.84) * mm});
            skPoint(sketch, "E158.visualSharp", {"position": v(184.73, -120) * mm});
            skArc(sketch, "E158.filletArc", {"start": v(184.73, -115) * mm, "mid": v(186.2, -118.54) * mm, "end": v(189.73, -120) * mm});
            skPoint(sketch, "E159.visualSharp", {"position": v(196.73, -120) * mm});
            skArc(sketch, "E159.filletArc", {"start": v(191.73, -120) * mm, "mid": v(195.27, -118.54) * mm, "end": v(196.73, -115) * mm});
            skLineSegment(sketch, "E160", {"start": v(196.73, -100) * mm, "end": v(191.73, -100) * mm});
            skLineSegment(sketch, "E161", {"start": v(191.73, -100) * mm, "end": v(191.73, -108) * mm});
            skLineSegment(sketch, "E162", {"start": v(191.73, -108) * mm, "end": v(196.73, -108) * mm});
            skSolve(sketch);
        }
        {
            var Q0;
            Q0 = qSketchRegion(id + "F29", true);
            extrude(context, id + "F30", {"entities" : qUnion([Q0]), "depth" : 8 * mm, "offsetDistance" : 25 * mm});
        }
        {
            var Q0;
            Q0=makeQuery(id+"F25.opExtrude","SWEPT_BODY",BODY,{"disambiguationData":[OSD([sQuery(id+"F24.wireOp",EDGE,"E110"),sQuery(id+"F24.wireOp",EDGE,"E111"),sQuery(id+"F24.wireOp",EDGE,"E112"),sQuery(id+"F24.wireOp",EDGE,"E113.MirrorCS"),sQuery(id+"F24.wireOp",EDGE,"E114.MirrorCS"),sQuery(id+"F24.wireOp",EDGE,"E115.MirrorCS"),sQuery(id+"F24.wireOp",EDGE,"E116.1.1"),sQuery(id+"F24.wireOp",EDGE,"E116.1.2"),sQuery(id+"F24.wireOp",EDGE,"E116.1.3"),sQuery(id+"F24.wireOp",EDGE,"E116.1.4"),sQuery(id+"F24.wireOp",EDGE,"E116.1.5"),sQuery(id+"F24.wireOp",EDGE,"E116.1.6"),sQuery(id+"F24.wireOp",EDGE,"E108"),sQuery(id+"F24.wireOp",EDGE,"E116.2.1"),sQuery(id+"F24.wireOp",EDGE,"E116.2.2"),sQuery(id+"F24.wireOp",EDGE,"E116.2.3"),sQuery(id+"F24.wireOp",EDGE,"E116.2.4"),sQuery(id+"F24.wireOp",EDGE,"E116.2.5"),sQuery(id+"F24.wireOp",EDGE,"E116.2.6"),sQuery(id+"F24.wireOp",EDGE,"E117"),sQuery(id+"F24.wireOp",EDGE,"E118.trimOffspring"),sQuery(id+"F24.wireOp",EDGE,"E119.trimOffspring"),sQuery(id+"F24.wireOp",EDGE,"E120.trimOffspring"),sQuery(id+"F24.wireOp",EDGE,"E121.trimOffspring"),sQuery(id+"F24.wireOp",EDGE,"E122.trimOffspring")])]});
            transform(context, id + "F31", {"entities" : qUnion([Q0]), "transformType" : TransformType.TRANSLATION_3D, "dx" : 2 * mm, "dy" : 0 * mm, "dz" : 0 * mm, "makeCopy" : false});
        }
        {
            var Q0;
            Q0=makeQuery(id+"F28.opExtrude","SWEPT_BODY",BODY,{"disambiguationData":[OSD([sQuery(id+"F27.wireOp",EDGE,"E123"),sQuery(id+"F27.wireOp",EDGE,"E125.0"),sQuery(id+"F27.wireOp",EDGE,"E126.0.12"),sQuery(id+"F27.wireOp",EDGE,"E126.0.13"),sQuery(id+"F27.wireOp",EDGE,"E126.0.15"),sQuery(id+"F27.wireOp",EDGE,"E127"),sQuery(id+"F27.wireOp",EDGE,"E128"),sQuery(id+"F27.wireOp",EDGE,"E129.1.0"),sQuery(id+"F27.wireOp",EDGE,"E129.1.1"),sQuery(id+"F27.wireOp",EDGE,"E129.1.2"),sQuery(id+"F27.wireOp",EDGE,"E129.1.3"),sQuery(id+"F27.wireOp",EDGE,"E129.1.4"),sQuery(id+"F27.wireOp",EDGE,"E129.1.5"),sQuery(id+"F27.wireOp",EDGE,"E129.2.0"),sQuery(id+"F27.wireOp",EDGE,"E129.2.1"),sQuery(id+"F27.wireOp",EDGE,"E129.2.2"),sQuery(id+"F27.wireOp",EDGE,"E129.2.3"),sQuery(id+"F27.wireOp",EDGE,"E129.2.4"),sQuery(id+"F27.wireOp",EDGE,"E129.2.5"),sQuery(id+"F27.wireOp",EDGE,"E130.0"),sQuery(id+"F27.wireOp",EDGE,"E131.trimOffspring"),sQuery(id+"F27.wireOp",EDGE,"E132.trimOffspring"),sQuery(id+"F27.wireOp",EDGE,"E133.trimOffspring"),sQuery(id+"F27.wireOp",EDGE,"E134.trimOffspring"),sQuery(id+"F27.wireOp",EDGE,"E135.trimOffspring")])]});
            transform(context, id + "F32", {"entities" : qUnion([Q0]), "transformType" : TransformType.TRANSLATION_3D, "dx" : 2 * mm, "dy" : 0 * mm, "dz" : 0 * mm, "makeCopy" : false});
        }
        {
            var Q0;
            Q0=makeQuery(id+"F30.opExtrude","SWEPT_BODY",BODY,{"disambiguationData":[OSD([sQuery(id+"F29.wireOp",EDGE,"E136.top"),sQuery(id+"F29.wireOp",EDGE,"E136.left"),sQuery(id+"F29.wireOp",EDGE,"E136.right"),sQuery(id+"F29.wireOp",EDGE,"E137.MirrorC"),sQuery(id+"F29.wireOp",EDGE,"E138.filletArc"),sQuery(id+"F29.wireOp",EDGE,"E139.filletArc"),sQuery(id+"F29.wireOp",EDGE,"E141"),sQuery(id+"F29.wireOp",EDGE,"E142.trimOffspring"),sQuery(id+"F29.wireOp",EDGE,"E144"),sQuery(id+"F29.wireOp",EDGE,"E145"),sQuery(id+"F29.wireOp",EDGE,"E146"),sQuery(id+"F29.wireOp",EDGE,"E147"),sQuery(id+"F29.wireOp",EDGE,"E148"),sQuery(id+"F29.wireOp",EDGE,"E149"),sQuery(id+"F29.wireOp",EDGE,"E150"),sQuery(id+"F29.wireOp",EDGE,"E151"),sQuery(id+"F29.wireOp",EDGE,"E152"),sQuery(id+"F29.wireOp",EDGE,"E153"),sQuery(id+"F29.wireOp",EDGE,"E154.filletArc"),sQuery(id+"F29.wireOp",EDGE,"E155.filletArc"),sQuery(id+"F29.wireOp",EDGE,"E156.filletArc"),sQuery(id+"F29.wireOp",EDGE,"E157.filletArc"),sQuery(id+"F29.wireOp",EDGE,"E158.filletArc"),sQuery(id+"F29.wireOp",EDGE,"E159.filletArc"),sQuery(id+"F29.wireOp",EDGE,"E160"),sQuery(id+"F29.wireOp",EDGE,"E161"),sQuery(id+"F29.wireOp",EDGE,"E162")])]});
            var Q1;
            Q1=qCreatedBy(makeId("Front.planeOp"),FACE);
            mirror(context, id + "F33", {"entities" : qUnion([Q0]), "mirrorPlane" : qUnion([Q1])});
        }
        {
            var Q0;
            Q0=makeQuery(id+"F25.opExtrude","SWEPT_FACE",FACE,{"disambiguationData":[OSD([sQuery(id+"F24.wireOp",EDGE,"E116.1.6")])]});
            var sketch = newSketch(context, id + "F34", { "sketchPlane" : qUnion([Q0])});
            skPoint(sketch, "E163.MirrorP", {"position": v(-134.97, 12.85) * mm});
            skPoint(sketch, "E164.start.orphan", {"position": v(-96.79, 100) * mm});
            skLineSegment(sketch, "E165", {"start": v(-171.79, 100) * mm, "end": v(-171.79, 115) * mm});
            skLineSegment(sketch, "E166", {"start": v(-166.79, 120) * mm, "end": v(-164.79, 120) * mm});
            skLineSegment(sketch, "E167", {"start": v(-159.79, 115) * mm, "end": v(-159.79, 108) * mm});
            skLineSegment(sketch, "E168", {"start": v(-159.79, 100) * mm, "end": v(-195.05, -100) * mm});
            skLineSegment(sketch, "E169", {"start": v(-195.05, -108) * mm, "end": v(-195.05, -115) * mm});
            skLineSegment(sketch, "E170", {"start": v(-200.05, -120) * mm, "end": v(-202.05, -120) * mm});
            skLineSegment(sketch, "E171", {"start": v(-207.05, -100) * mm, "end": v(-207.05, -115) * mm});
            skLineSegment(sketch, "E172", {"start": v(-159.79, 108) * mm, "end": v(-164.79, 108) * mm});
            skLineSegment(sketch, "E173", {"start": v(-164.79, 108) * mm, "end": v(-164.79, 100) * mm});
            skLineSegment(sketch, "E174", {"start": v(-164.79, 100) * mm, "end": v(-159.79, 100) * mm});
            skPoint(sketch, "E175.visualSharp", {"position": v(-171.79, 120) * mm});
            skArc(sketch, "E175.filletArc", {"start": v(-166.79, 120) * mm, "mid": v(-170.32, 118.54) * mm, "end": v(-171.79, 115) * mm});
            skPoint(sketch, "E176.visualSharp", {"position": v(-159.79, 120) * mm});
            skArc(sketch, "E176.filletArc", {"start": v(-159.79, 115) * mm, "mid": v(-161.25, 118.54) * mm, "end": v(-164.79, 120) * mm});
            skPoint(sketch, "E177.visualSharp", {"position": v(-207.05, -120) * mm});
            skArc(sketch, "E177.filletArc", {"start": v(-207.05, -115) * mm, "mid": v(-205.59, -118.54) * mm, "end": v(-202.05, -120) * mm});
            skPoint(sketch, "E178.visualSharp", {"position": v(-195.05, -120) * mm});
            skArc(sketch, "E178.filletArc", {"start": v(-200.05, -120) * mm, "mid": v(-196.52, -118.54) * mm, "end": v(-195.05, -115) * mm});
            skLineSegment(sketch, "E179", {"start": v(-195.05, -100) * mm, "end": v(-200.05, -100) * mm});
            skLineSegment(sketch, "E180", {"start": v(-200.05, -100) * mm, "end": v(-200.05, -108) * mm});
            skLineSegment(sketch, "E181", {"start": v(-200.05, -108) * mm, "end": v(-195.05, -108) * mm});
            skLineSegment(sketch, "E182", {"start": v(-171.79, 100) * mm, "end": v(-207.05, -100) * mm});
            skSolve(sketch);
        }
        {
            var Q0;
            Q0 = qSketchRegion(id + "F34", true);
            extrude(context, id + "F35", {"entities" : qUnion([Q0]), "depth" : 8 * mm, "offsetDistance" : 25 * mm});
        }
        {
            var Q0;
            Q0=makeQuery(id+"F25.opExtrude","SWEPT_FACE",FACE,{"disambiguationData":[OSD([sQuery(id+"F24.wireOp",EDGE,"E116.2.6")])]});
            var sketch = newSketch(context, id + "F36", { "sketchPlane" : qUnion([Q0])});
            skLineSegment(sketch, "E183", {"start": v(-171.79, 100) * mm, "end": v(-171.79, 115) * mm});
            skLineSegment(sketch, "E184", {"start": v(-166.79, 120) * mm, "end": v(-164.79, 120) * mm});
            skLineSegment(sketch, "E185", {"start": v(-159.79, 115) * mm, "end": v(-159.79, 108) * mm});
            skLineSegment(sketch, "E186", {"start": v(-159.79, 100) * mm, "end": v(-195.05, -100) * mm});
            skLineSegment(sketch, "E187", {"start": v(-195.05, -108) * mm, "end": v(-195.05, -115) * mm});
            skLineSegment(sketch, "E188", {"start": v(-200.05, -120) * mm, "end": v(-202.05, -120) * mm});
            skLineSegment(sketch, "E189", {"start": v(-207.05, -100) * mm, "end": v(-207.05, -115) * mm});
            skLineSegment(sketch, "E190", {"start": v(-159.79, 108) * mm, "end": v(-164.79, 108) * mm});
            skLineSegment(sketch, "E191", {"start": v(-164.79, 108) * mm, "end": v(-164.79, 100) * mm});
            skLineSegment(sketch, "E192", {"start": v(-164.79, 100) * mm, "end": v(-159.79, 100) * mm});
            skPoint(sketch, "E193.visualSharp", {"position": v(-171.79, 120) * mm});
            skArc(sketch, "E193.filletArc", {"start": v(-166.79, 120) * mm, "mid": v(-170.32, 118.54) * mm, "end": v(-171.79, 115) * mm});
            skPoint(sketch, "E194.visualSharp", {"position": v(-159.79, 120) * mm});
            skArc(sketch, "E194.filletArc", {"start": v(-159.79, 115) * mm, "mid": v(-161.25, 118.54) * mm, "end": v(-164.79, 120) * mm});
            skPoint(sketch, "E195.visualSharp", {"position": v(-207.05, -120) * mm});
            skArc(sketch, "E195.filletArc", {"start": v(-207.05, -115) * mm, "mid": v(-205.59, -118.54) * mm, "end": v(-202.05, -120) * mm});
            skPoint(sketch, "E196.visualSharp", {"position": v(-195.05, -120) * mm});
            skArc(sketch, "E196.filletArc", {"start": v(-200.05, -120) * mm, "mid": v(-196.52, -118.54) * mm, "end": v(-195.05, -115) * mm});
            skLineSegment(sketch, "E197", {"start": v(-195.05, -100) * mm, "end": v(-200.05, -100) * mm});
            skLineSegment(sketch, "E198", {"start": v(-200.05, -100) * mm, "end": v(-200.05, -108) * mm});
            skLineSegment(sketch, "E199", {"start": v(-200.05, -108) * mm, "end": v(-195.05, -108) * mm});
            skLineSegment(sketch, "E200", {"start": v(-171.79, 100) * mm, "end": v(-207.05, -100) * mm});
            skSolve(sketch);
        }
        {
            var Q0;
            Q0 = qSketchRegion(id + "F36", true);
            extrude(context, id + "F37", {"entities" : qUnion([Q0]), "depth" : 8 * mm, "offsetDistance" : 25 * mm});
        }
        {
            var Q0;
            Q0=makeQuery(id+"F25.opExtrude","SWEPT_FACE",FACE,{"disambiguationData":[OSD([sQuery(id+"F24.wireOp",EDGE,"E116.1.2")])]});
            cPlane(context, id + "F38", {"entities" : qUnion([Q0]), "cplaneType" : CPlaneType.OFFSET, "offset" : 8 * mm, "oppositeDirection" : true, "width" : 150 * mm, "height" : 150 * mm});
        }
        {
            var Q0;
            Q0=makeQuery(id+"F35.opExtrude","SWEPT_BODY",BODY,{"disambiguationData":[OSD([sQuery(id+"F34.wireOp",EDGE,"E165"),sQuery(id+"F34.wireOp",EDGE,"E166"),sQuery(id+"F34.wireOp",EDGE,"E167"),sQuery(id+"F34.wireOp",EDGE,"E168"),sQuery(id+"F34.wireOp",EDGE,"E169"),sQuery(id+"F34.wireOp",EDGE,"E170"),sQuery(id+"F34.wireOp",EDGE,"E171"),sQuery(id+"F34.wireOp",EDGE,"E172"),sQuery(id+"F34.wireOp",EDGE,"E173"),sQuery(id+"F34.wireOp",EDGE,"E174"),sQuery(id+"F34.wireOp",EDGE,"E175.filletArc"),sQuery(id+"F34.wireOp",EDGE,"E176.filletArc"),sQuery(id+"F34.wireOp",EDGE,"E177.filletArc"),sQuery(id+"F34.wireOp",EDGE,"E178.filletArc"),sQuery(id+"F34.wireOp",EDGE,"E179"),sQuery(id+"F34.wireOp",EDGE,"E180"),sQuery(id+"F34.wireOp",EDGE,"E181"),sQuery(id+"F34.wireOp",EDGE,"E182")])]});
            var Q1;
            Q1=qCreatedBy(id+"F38.planeOp",FACE);
            mirror(context, id + "F39", {"entities" : qUnion([Q0]), "mirrorPlane" : qUnion([Q1])});
        }
        {
            var Q0;
            Q0=makeQuery(id+"F25.opExtrude","SWEPT_FACE",FACE,{"disambiguationData":[OSD([sQuery(id+"F24.wireOp",EDGE,"E116.2.2")])]});
            cPlane(context, id + "F40", {"entities" : qUnion([Q0]), "cplaneType" : CPlaneType.OFFSET, "offset" : 8 * mm, "oppositeDirection" : true, "width" : 150 * mm, "height" : 150 * mm});
        }
        {
            var Q0;
            Q0=makeQuery(id+"F37.opExtrude","SWEPT_BODY",BODY,{"disambiguationData":[OSD([sQuery(id+"F36.wireOp",EDGE,"E183"),sQuery(id+"F36.wireOp",EDGE,"E184"),sQuery(id+"F36.wireOp",EDGE,"E185"),sQuery(id+"F36.wireOp",EDGE,"E186"),sQuery(id+"F36.wireOp",EDGE,"E187"),sQuery(id+"F36.wireOp",EDGE,"E188"),sQuery(id+"F36.wireOp",EDGE,"E189"),sQuery(id+"F36.wireOp",EDGE,"E190"),sQuery(id+"F36.wireOp",EDGE,"E191"),sQuery(id+"F36.wireOp",EDGE,"E192"),sQuery(id+"F36.wireOp",EDGE,"E193.filletArc"),sQuery(id+"F36.wireOp",EDGE,"E194.filletArc"),sQuery(id+"F36.wireOp",EDGE,"E195.filletArc"),sQuery(id+"F36.wireOp",EDGE,"E196.filletArc"),sQuery(id+"F36.wireOp",EDGE,"E197"),sQuery(id+"F36.wireOp",EDGE,"E198"),sQuery(id+"F36.wireOp",EDGE,"E199"),sQuery(id+"F36.wireOp",EDGE,"E200")])]});
            var Q1;
            Q1=qCreatedBy(id+"F40.planeOp",FACE);
            mirror(context, id + "F41", {"entities" : qUnion([Q0]), "mirrorPlane" : qUnion([Q1])});
        }
    });
